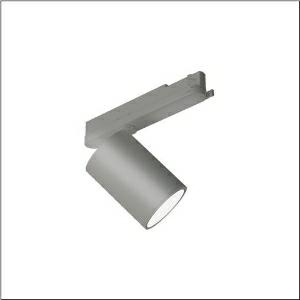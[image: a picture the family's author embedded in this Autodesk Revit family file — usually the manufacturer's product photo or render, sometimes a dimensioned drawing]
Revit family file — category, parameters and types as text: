
# Revit family: spot_31_51sf62mab4b
name_source: partatom
category: Lighting Fixtures
units: mm (PartAtom-declared; Revit-internal decimal feet)

## family parameters
Cut with Voids When Loaded = No
Host = Face
Light Source = No
Part Type = Normal
Room Calculation Point = No
Round Connector Dimension = Use Diameter
Shared = No

## types (1)
- --- (1 x LED, 4980 lm, 41.8 W, 3000K)
    Apparent Load = 42 VA
    CIE Flux Codes = 93 97 99 100 100
    Color Rendering = 90
    Color Temperature = 3000K
    Default Elevation = 1800 mm
    Description = Spot 31, directional spotlight, light control with lens, of PMMA, LED rated luminous flux: 4.790lm, light colour: 930, control gear: ECG Multilumen, with 3-phase adapter, mains connection: 220..240V, AC, 50/60Hz, of aluminium, metallic grey (RAL 9006), length: 213mm, diameter: 90mm, protection rating (complete): IP20, insulation class (complete): insulation class I (protective earthing), certification: CE, impact resistance: IK02, permissible ambient temperature for indoor applications: -20..+40°C, packaging unit: 1 piece
    Height = 175 mm
    Lamp = 1 x LED
    Lamp Light Flux = 4980 lm
    Lamp Power = 41.8 W
    Lamp count = 1
    Length = 90 mm
    Luminous efficacy = 119 lm/W
    Manufacturer = Siteco
    ModVariant = No
    Model = 51SF62MAB4B
    Mounting Place = Ceiling
    Mounting Type = Pendant
    Number of Poles = 1
    OnlyDefault = Yes
    Power Factor = 1
    Product Name = Spot 31
    Product group = directional spotlight
    ProductGroupID = 905
    Protection Class = Protection class I
    Protection Degree = IP 20
    RLX_Detail_Level = 1
    RLX_Emergency_Light_Flux = 0 lm
    RLX_Emergency_Type = 0
    RLX_Emergency_Type_DB = No
    RlxData = <blob elided: 20053 chars, md5=13796689>
    Socket = socket
    Standby Power = 0 W
    System Light Flux = 4980 lm
    System Power = 42 W
    Type Comments = factory setting: luminous flux: 100 % | (ON | ON | ON | ON) | 1050 mA
    Type Image = l_1273725.jpg
    URL = http://relux.com
    VarID = @adj_146065
    Voltage = 0 V
    Weight = 0.00 kg
    Width = 0 mm  [stored 0 ft]

note: [stored X ft] marks values corroborated as IEEE doubles in the binary element streams (Revit-internal decimal feet)

## geometry (parser evidence)
native form markers: Blend x4, Sweep x10
no freeform markers — native parametric forms only
